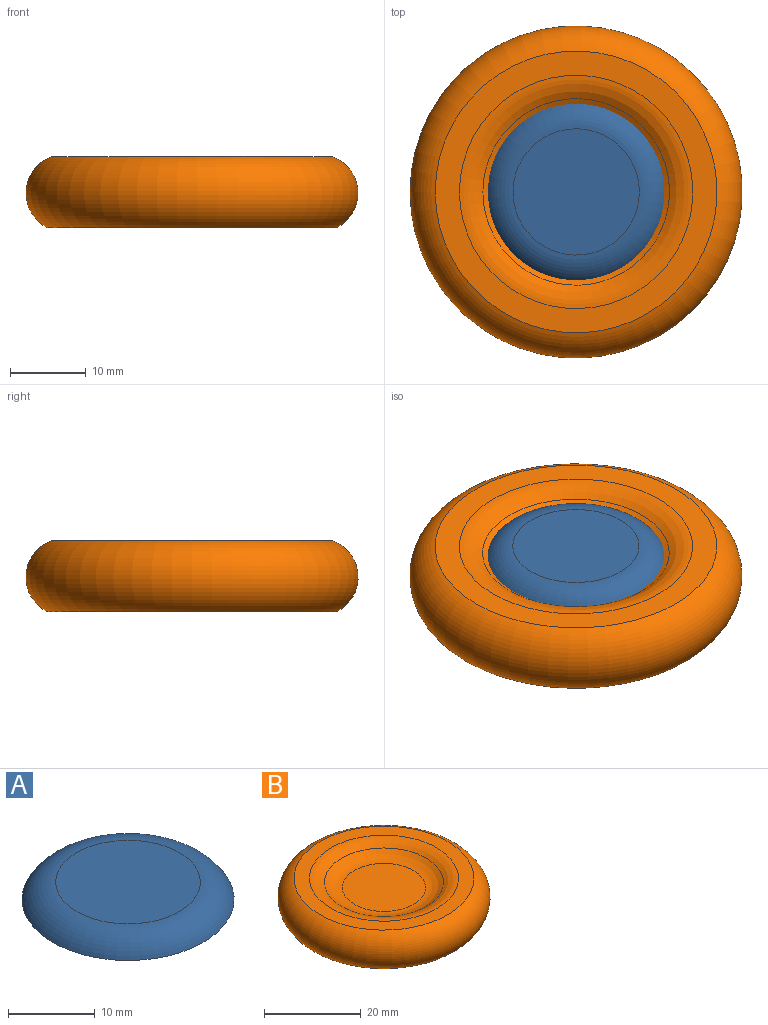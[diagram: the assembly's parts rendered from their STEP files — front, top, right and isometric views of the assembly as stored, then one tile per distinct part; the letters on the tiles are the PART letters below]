
ASSEMBLY  parts=2 mates=1
PART A: 3 faces, bbox 27.4x27.4x4.3 mm
  f0: torus R=8.32mm, axis (0,0,1), area 316.8mm2, adj f1,f2
  f1: plane 16.63x16.63mm, normal (0,0,1), area 217.3mm2, adj f0
  f2: plane 24.38x24.38mm, normal (0,0,-1), area 467mm2, adj f0
PART B: 6 faces, bbox 47.4x47.4x10.2 mm
  f0: torus R=8.59mm, axis (0,0,-1), area 263.4mm2, adj f1,f5
  f1: plane 17.17x17.17mm, normal (0,0,1), area 231.6mm2, adj f0
  f2: plane 38.1x38.1mm, normal (0,0,-1), area 1140.1mm2, adj f3
  f3: torus R=16.8mm, axis (0,0,-1), area 1547.2mm2, adj f2,f4
  f4: plane 37.12x37.12mm, normal (0,0,1), area 340mm2, adj f3,f5
  f5: torus R=15.37mm, axis (0,0,-1), area 287mm2, adj f0,f4
PLACE A t=(-8.06,-0.33,8.77)mm
PLACE B t=(-8.06,-0.33,1.78)mm
MATE planar A.f0 <-> B.f0  axis (0,0,-1) through (-8.06,-0.33,8.77)mm
